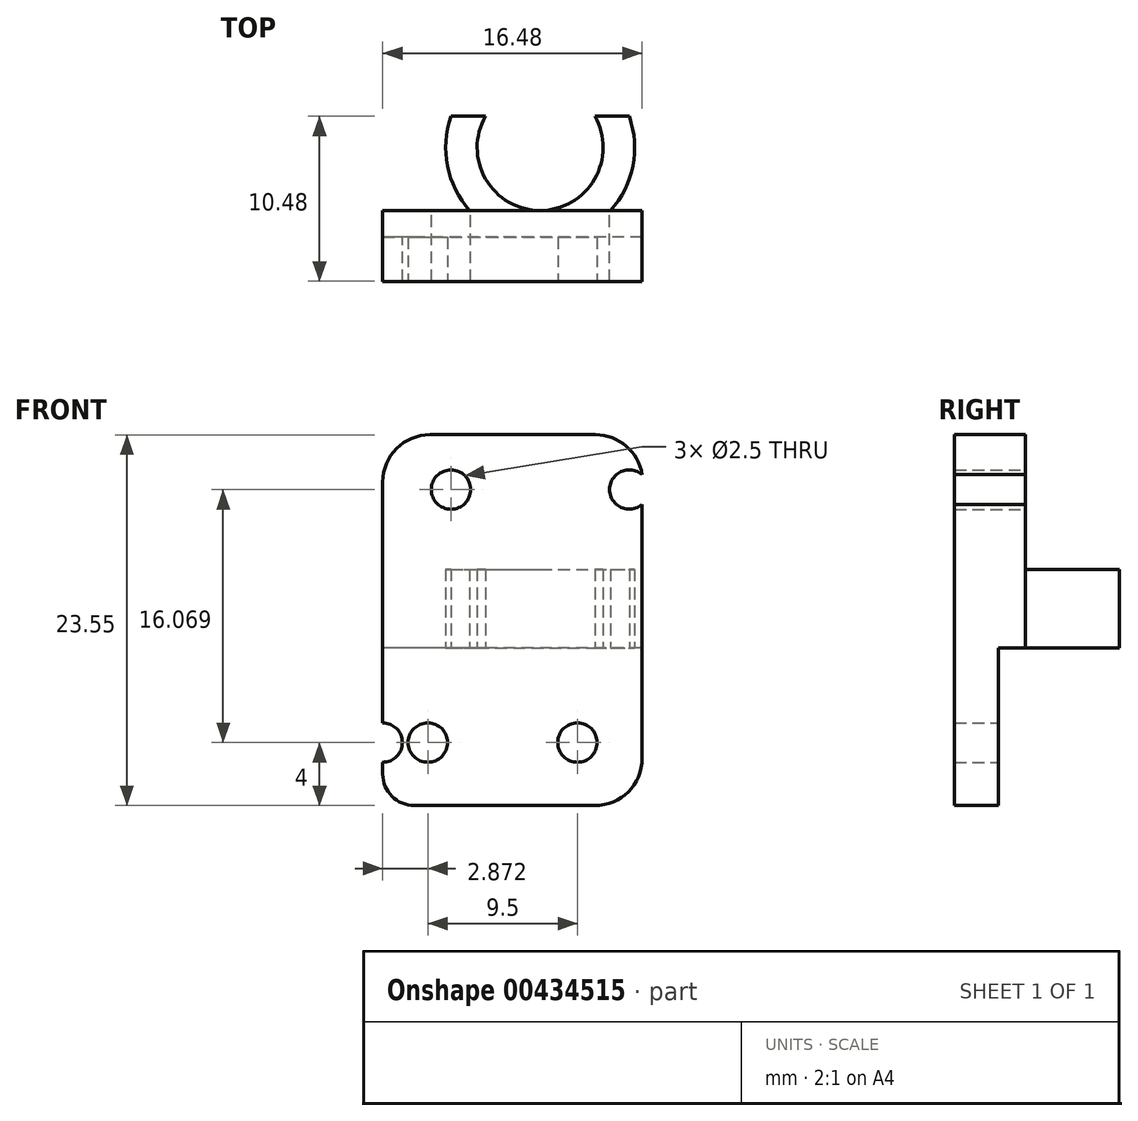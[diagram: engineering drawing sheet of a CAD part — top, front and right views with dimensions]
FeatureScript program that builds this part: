
annotation { "Feature Type Name" : "Feature", "Feature Type Description" : "" }
export const myFeature = defineFeature(function(context is Context, id is Id, definition is map)
    precondition{}
    {
        {
            var Q0;
            Q0=qCreatedBy(makeId("Top.planeOp"),FACE);
            var sketch = newSketch(context, id + "F0", { "sketchPlane" : qUnion([Q0])});
            skArc(sketch, "E0", {"start": v(-19.61, 7.8) * mm, "mid": v(-13.95, -0.17) * mm, "end": v(-8.28, 7.8) * mm});
            skLineSegment(sketch, "E1.right", {"start": v(278.54, 89.36) * mm, "end": v(278.54, 0) * mm});
            skArc(sketch, "E2", {"start": v(-17.42, 7.8) * mm, "mid": v(-13.95, 1.83) * mm, "end": v(-10.47, 7.8) * mm});
            skLineSegment(sketch, "E3.top", {"start": v(-19.61, 7.8) * mm, "end": v(-17.42, 7.8) * mm});
            skLineSegment(sketch, "E4.trimOffspring", {"start": v(-10.47, 7.8) * mm, "end": v(-8.28, 7.8) * mm});
            skPoint(sketch, "E5", {"position": v(-13.95, -1.45) * mm});
            skLineSegment(sketch, "E6", {"start": v(-13.95, 7.55) * mm, "end": v(-13.95, -10.44) * mm, "construction": true});
            skPoint(sketch, "E7.startSnap0", {"position": v(-13.95, 1.83) * mm});
            skSolve(sketch);
        }
        {
            var Q0;
            Q0=qSketchRegion(id+"F0",true);
            extrude(context, id + "F1", {"entities" : qUnion([Q0]), "depth" : 20 * mm});
        }
        {
            var Q0;
            Q0=qCreatedBy(makeId("Top.planeOp"),FACE);
            var sketch = newSketch(context, id + "F2", { "sketchPlane" : qUnion([Q0])});
            skArc(sketch, "E8.0.0", {"start": v(-17.42, 7.8) * mm, "mid": v(-13.95, 1.83) * mm, "end": v(-10.47, 7.8) * mm, "construction": true});
            skLineSegment(sketch, "E8.0.1", {"start": v(-10.47, 7.8) * mm, "end": v(-8.28, 7.8) * mm, "construction": true});
            skArc(sketch, "E8.0.2", {"start": v(-8.28, 7.8) * mm, "mid": v(-13.95, -0.17) * mm, "end": v(-19.61, 7.8) * mm, "construction": true});
            skLineSegment(sketch, "E8.0.3", {"start": v(-19.61, 7.8) * mm, "end": v(-17.42, 7.8) * mm, "construction": true});
            skPoint(sketch, "E9", {"position": v(-13.95, -0.17) * mm});
            skPoint(sketch, "E10", {"position": v(-13.95, 1.83) * mm});
            skLineSegment(sketch, "E11", {"start": v(-13.95, 1.83) * mm, "end": v(-3.95, 1.83) * mm});
            skLineSegment(sketch, "E12", {"start": v(-3.95, 1.83) * mm, "end": v(-3.95, -1.17) * mm});
            skLineSegment(sketch, "E13", {"start": v(-3.95, -1.17) * mm, "end": v(-23.95, -1.17) * mm});
            skLineSegment(sketch, "E14", {"start": v(-23.95, -1.17) * mm, "end": v(-23.95, 1.83) * mm});
            skLineSegment(sketch, "E15", {"start": v(-23.95, 1.83) * mm, "end": v(-13.95, 1.83) * mm});
            skSolve(sketch);
        }
        {
            var Q0;
            Q0=makeQuery(id+"F2.imprint","IMPRINT",FACE,{"disambiguationData":[TD([[makeQuery(id+"F2.imprint","IMPRINT",EDGE,{"derivedFrom":sQuery(id+"F2.wireOp",EDGE,"E11")}),-1.0]])]});
            extrude(context, id + "F3", {"entities" : qUnion([Q0]), "operationType" : NewBodyOperationType.ADD, "endBound" : BoundingType.SYMMETRIC, "depth" : 20 * mm});
        }
        {
            var Q0;
            Q0=qCreatedBy(makeId("Front.planeOp"),FACE);
            var sketch = newSketch(context, id + "F4", { "sketchPlane" : qUnion([Q0])});
            skCircle(sketch, "E16", {"center": v(-11.58, -6) * mm, "radius": 1.25 * mm});
            skPoint(sketch, "E17", {"position": v(-10.9, 30) * mm});
            skPoint(sketch, "E18.endSnap0", {"position": v(-14.04, 0) * mm});
            skLineSegment(sketch, "E19.0", {"start": v(-23.95, -10) * mm, "end": v(-3.95, -10) * mm, "construction": true});
            skPoint(sketch, "E20", {"position": v(-13.95, -10) * mm});
            skLineSegment(sketch, "E21", {"start": v(-13.95, -10) * mm, "end": v(-13.95, -0.98) * mm, "construction": true});
            skCircle(sketch, "E22.MirrorC", {"center": v(-21.08, -6) * mm, "radius": 1.25 * mm});
            skLineSegment(sketch, "E23", {"start": v(-21.08, -6) * mm, "end": v(-1.03, -6) * mm, "construction": true});
            skSolve(sketch);
        }
        {
            var Q0;
            Q0=qSketchRegion(id+"F4",true);
            extrude(context, id + "F5", {"entities" : qUnion([Q0]), "operationType" : NewBodyOperationType.REMOVE, "endBound" : BoundingType.SYMMETRIC, "oppositeDirection" : true, "depth" : 4.4 * mm});
        }
        {
            var Q0;
            Q0=makeQuery(id+"F3.opExtrude","CAP_FACE",FACE,{"disambiguationData":[OSD([sQuery(id+"F2.wireOp",EDGE,"E11"),sQuery(id+"F2.wireOp",EDGE,"E12"),sQuery(id+"F2.wireOp",EDGE,"E13"),sQuery(id+"F2.wireOp",EDGE,"E14"),sQuery(id+"F2.wireOp",EDGE,"E15")])],"isStart":false});
            var sketch = newSketch(context, id + "F6", { "sketchPlane" : qUnion([Q0])});
            skArc(sketch, "E24.0.0", {"start": v(-9.48, 1.83) * mm, "mid": v(-13.95, -0.17) * mm, "end": v(-18.42, 1.83) * mm});
            skLineSegment(sketch, "E24.0.1", {"start": v(-18.42, 1.83) * mm, "end": v(-23.95, 1.83) * mm});
            skLineSegment(sketch, "E24.0.2", {"start": v(-23.95, 1.83) * mm, "end": v(-23.95, -1.17) * mm});
            skLineSegment(sketch, "E24.0.3", {"start": v(-23.95, -1.17) * mm, "end": v(-3.95, -1.17) * mm});
            skLineSegment(sketch, "E24.0.4", {"start": v(-3.95, -1.17) * mm, "end": v(-3.95, 1.83) * mm});
            skLineSegment(sketch, "E24.0.5", {"start": v(-3.95, 1.83) * mm, "end": v(-9.48, 1.83) * mm});
            skSolve(sketch);
        }
        {
            var Q0;
            Q0=qSketchRegion(id+"F6",true);
            var Q1;
            Q1=makeQuery(id+"F1.opExtrude","CAP_FACE",FACE,{"disambiguationData":[OSD([sQuery(id+"F0.wireOp",EDGE,"E0"),sQuery(id+"F0.wireOp",EDGE,"E2"),sQuery(id+"F0.wireOp",EDGE,"E3.top"),sQuery(id+"F0.wireOp",EDGE,"E4.trimOffspring")])],"isStart":false});
            extrude(context, id + "F7", {"entities" : qUnion([Q0]), "operationType" : NewBodyOperationType.ADD, "endBound" : BoundingType.UP_TO_SURFACE, "endBoundEntityFace" : qUnion([Q1]), "depth" : 6.4 * mm});
        }
        {
            var Q0;
            Q0=makeQuery(id+"F7.boolean.opBoolean","MERGE",FACE,{"derivedFrom":[makeQuery(id+"F3.opExtrude","SWEPT_FACE",FACE,{"disambiguationData":[OSD([sQuery(id+"F2.wireOp",EDGE,"E11"),sQuery(id+"F2.wireOp",EDGE,"E15")])]}),makeQuery(id+"F7.opExtrude","SWEPT_FACE",FACE,{"disambiguationData":[OSD([sQuery(id+"F6.wireOp",EDGE,"E24.0.1")])]}),makeQuery(id+"F7.opExtrude","SWEPT_FACE",FACE,{"disambiguationData":[OSD([sQuery(id+"F6.wireOp",EDGE,"E24.0.5")])]})]});
            cPlane(context, id + "F8", {"entities" : qUnion([Q0]), "cplaneType" : CPlaneType.OFFSET, "offset" : 25 * mm, "width" : 150 * mm, "height" : 150 * mm});
        }
        {
            var Q0;
            Q0=qCreatedBy(id+"F8.planeOp",FACE);
            var sketch = newSketch(context, id + "F9", { "sketchPlane" : qUnion([Q0])});
            skPoint(sketch, "E25.0", {"position": v(21.08, -6) * mm});
            skPoint(sketch, "E26.0", {"position": v(11.58, -6) * mm});
            skLineSegment(sketch, "E27", {"start": v(1.82, -6) * mm, "end": v(28.97, -6) * mm, "construction": true});
            skLineSegment(sketch, "E28.0", {"start": v(3.95, 20) * mm, "end": v(3.95, -10) * mm, "construction": true});
            skLineSegment(sketch, "E29.0", {"start": v(23.95, 20) * mm, "end": v(23.95, -10) * mm, "construction": true});
            skPoint(sketch, "E30", {"position": v(3.95, -6) * mm});
            skPoint(sketch, "E31", {"position": v(23.95, -6) * mm});
            skCircle(sketch, "E32.0", {"center": v(11.58, -6) * mm, "radius": 1.25 * mm, "construction": true});
            skCircle(sketch, "E33", {"center": v(23.95, -6) * mm, "radius": 1.25 * mm});
            skCircle(sketch, "E34.MirrorC", {"center": v(3.95, -6) * mm, "radius": 1.25 * mm});
            skSolve(sketch);
        }
        {
            var Q0;
            Q0=qSketchRegion(id+"F9",true);
            extrude(context, id + "F10", {"entities" : qUnion([Q0]), "operationType" : NewBodyOperationType.REMOVE, "endBound" : BoundingType.THROUGH_ALL, "oppositeDirection" : true, "depth" : 25 * mm});
        }
        {
            var Q0;
            Q0=makeQuery(id+"F3.opExtrude","CAP_EDGE",EDGE,{"disambiguationData":[OSD([sQuery(id+"F2.wireOp",EDGE,"E14")])],"isStart":true});
            var Q1;
            Q1=makeQuery(id+"F3.opExtrude","CAP_EDGE",EDGE,{"disambiguationData":[OSD([sQuery(id+"F2.wireOp",EDGE,"E12")])],"isStart":true});
            fillet(context, id + "F11", {"entities" : qUnion([Q0, Q1]), "radius" : 2 * mm, "tangentPropagation" : true, "allowEdgeOverflow" : false});
        }
        {
            var Q0;
            Q0=makeQuery(id+"F7.boolean.opBoolean","MERGE",FACE,{"derivedFrom":[makeQuery(id+"F3.opExtrude","SWEPT_FACE",FACE,{"disambiguationData":[OSD([sQuery(id+"F2.wireOp",EDGE,"E13")])]}),makeQuery(id+"F7.opExtrude","SWEPT_FACE",FACE,{"disambiguationData":[OSD([sQuery(id+"F6.wireOp",EDGE,"E24.0.3")])]})]});
            cPlane(context, id + "F12", {"entities" : qUnion([Q0]), "cplaneType" : CPlaneType.OFFSET, "offset" : 0 * mm, "width" : 150 * mm, "height" : 150 * mm});
        }
        {
            var Q0;
            Q0=qCreatedBy(id+"F12.planeOp",FACE);
            var sketch = newSketch(context, id + "F13", { "sketchPlane" : qUnion([Q0])});
            skLineSegment(sketch, "E35.0.0", {"start": v(-23.95, -7.25) * mm, "end": v(-23.95, -8) * mm});
            skArc(sketch, "E35.0.1", {"start": v(-23.95, -8) * mm, "mid": v(-23.36, -9.41) * mm, "end": v(-21.95, -10) * mm});
            skLineSegment(sketch, "E35.0.2", {"start": v(-21.95, -10) * mm, "end": v(-5.95, -10) * mm});
            skArc(sketch, "E35.0.3", {"start": v(-5.95, -10) * mm, "mid": v(-4.53, -9.41) * mm, "end": v(-3.95, -8) * mm});
            skLineSegment(sketch, "E35.0.4", {"start": v(-3.95, -8) * mm, "end": v(-3.95, -7.25) * mm});
            skArc(sketch, "E35.0.5", {"start": v(-3.95, -7.25) * mm, "mid": v(-5.2, -6) * mm, "end": v(-3.95, -4.75) * mm});
            skLineSegment(sketch, "E35.0.6", {"start": v(-3.95, -4.75) * mm, "end": v(-3.95, 20) * mm});
            skLineSegment(sketch, "E35.0.7", {"start": v(-3.95, 20) * mm, "end": v(-23.95, 20) * mm});
            skLineSegment(sketch, "E35.0.8", {"start": v(-23.95, 20) * mm, "end": v(-23.95, -4.75) * mm});
            skArc(sketch, "E35.0.9", {"start": v(-23.95, -4.75) * mm, "mid": v(-22.7, -6) * mm, "end": v(-23.95, -7.25) * mm});
            skSolve(sketch);
        }
        {
            var Q0;
            Q0=qSketchRegion(id+"F13",true);
            extrude(context, id + "F14", {"entities" : qUnion([Q0]), "operationType" : NewBodyOperationType.ADD, "depth" : 1.5 * mm});
        }
        {
            var Q0;
            Q0=makeQuery(id+"F7.boolean.opBoolean","MERGE",FACE,{"derivedFrom":[makeQuery(id+"F3.opExtrude","SWEPT_FACE",FACE,{"disambiguationData":[OSD([sQuery(id+"F2.wireOp",EDGE,"E11"),sQuery(id+"F2.wireOp",EDGE,"E15")])]}),makeQuery(id+"F7.opExtrude","SWEPT_FACE",FACE,{"disambiguationData":[OSD([sQuery(id+"F6.wireOp",EDGE,"E24.0.1")])]}),makeQuery(id+"F7.opExtrude","SWEPT_FACE",FACE,{"disambiguationData":[OSD([sQuery(id+"F6.wireOp",EDGE,"E24.0.5")])]})]});
            cPlane(context, id + "F15", {"entities" : qUnion([Q0]), "cplaneType" : CPlaneType.OFFSET, "offset" : 0 * mm, "width" : 150 * mm, "height" : 150 * mm});
        }
        {
            var Q0;
            Q0=qCreatedBy(id+"F8.planeOp",FACE);
            var sketch = newSketch(context, id + "F16", { "sketchPlane" : qUnion([Q0])});
            skPoint(sketch, "E36.0", {"position": v(3.95, 0) * mm});
            skPoint(sketch, "E37.0", {"position": v(23.95, 0) * mm});
            skPoint(sketch, "E38.0", {"position": v(23.95, -10) * mm});
            skPoint(sketch, "E39.0", {"position": v(3.95, -10) * mm});
            skLineSegment(sketch, "E40", {"start": v(3.95, 0) * mm, "end": v(23.95, 0) * mm});
            skLineSegment(sketch, "E41", {"start": v(23.95, 0) * mm, "end": v(23.95, -10) * mm});
            skLineSegment(sketch, "E42", {"start": v(23.95, -10) * mm, "end": v(3.95, -10) * mm});
            skLineSegment(sketch, "E43", {"start": v(3.95, -10) * mm, "end": v(3.95, 0) * mm});
            skSolve(sketch);
        }
        {
            var Q0;
            Q0=qSketchRegion(id+"F16",true);
            extrude(context, id + "F17", {"entities" : qUnion([Q0]), "operationType" : NewBodyOperationType.REMOVE, "oppositeDirection" : true, "depth" : 26.7 * mm});
        }
        {
            var Q0;
            Q0=qCreatedBy(makeId("Front.planeOp"),FACE);
            cPlane(context, id + "F18", {"entities" : qUnion([Q0]), "cplaneType" : CPlaneType.OFFSET, "offset" : 25 * mm, "width" : 150 * mm, "height" : 150 * mm});
        }
        {
            var Q0;
            Q0=qCreatedBy(id+"F18.planeOp",FACE);
            var sketch = newSketch(context, id + "F19", { "sketchPlane" : qUnion([Q0])});
            skCircle(sketch, "E44.0", {"center": v(-11.58, -6) * mm, "radius": 1.25 * mm});
            skCircle(sketch, "E45.0", {"center": v(-21.08, -6) * mm, "radius": 1.25 * mm});
            skSolve(sketch);
        }
        {
            var Q0;
            Q0=qSketchRegion(id+"F19",true);
            extrude(context, id + "F20", {"entities" : qUnion([Q0]), "operationType" : NewBodyOperationType.REMOVE, "oppositeDirection" : true, "depth" : 32.1 * mm});
        }
        {
            var Q0;
            Q0=qCreatedBy(makeId("Top.planeOp"),FACE);
            cPlane(context, id + "F21", {"entities" : qUnion([Q0]), "cplaneType" : CPlaneType.OFFSET, "offset" : 11.9 * mm, "width" : 150 * mm, "height" : 150 * mm});
        }
        {
            var Q0;
            Q0=qCreatedBy(id+"F21.planeOp",FACE);
            var sketch = newSketch(context, id + "F22", { "sketchPlane" : qUnion([Q0])});
            skArc(sketch, "E46.0.0", {"start": v(-10.47, 7.8) * mm, "mid": v(-13.95, 1.83) * mm, "end": v(-17.42, 7.8) * mm, "construction": true});
            skLineSegment(sketch, "E46.0.1", {"start": v(-17.42, 7.8) * mm, "end": v(-19.61, 7.8) * mm, "construction": true});
            skArc(sketch, "E46.0.2", {"start": v(-19.61, 7.8) * mm, "mid": v(-19.83, 4.65) * mm, "end": v(-18.42, 1.83) * mm, "construction": true});
            skLineSegment(sketch, "E46.0.3", {"start": v(-18.42, 1.83) * mm, "end": v(-23.95, 1.83) * mm, "construction": true});
            skLineSegment(sketch, "E46.0.4", {"start": v(-23.95, 1.83) * mm, "end": v(-23.95, -2.67) * mm, "construction": true});
            skLineSegment(sketch, "E46.0.5", {"start": v(-23.95, -2.67) * mm, "end": v(-3.95, -2.67) * mm, "construction": true});
            skLineSegment(sketch, "E46.0.6", {"start": v(-3.95, -2.67) * mm, "end": v(-3.95, 1.83) * mm, "construction": true});
            skLineSegment(sketch, "E46.0.7", {"start": v(-3.95, 1.83) * mm, "end": v(-9.48, 1.83) * mm, "construction": true});
            skArc(sketch, "E46.0.8", {"start": v(-9.48, 1.83) * mm, "mid": v(-8.06, 4.65) * mm, "end": v(-8.28, 7.8) * mm, "construction": true});
            skLineSegment(sketch, "E46.0.9", {"start": v(-8.28, 7.8) * mm, "end": v(-10.47, 7.8) * mm, "construction": true});
            skLineSegment(sketch, "E47.bottom", {"start": v(-23.95, 1.83) * mm, "end": v(-3.95, 1.83) * mm});
            skLineSegment(sketch, "E47.top", {"start": v(-23.95, 11.1) * mm, "end": v(-3.95, 11.1) * mm});
            skLineSegment(sketch, "E47.left", {"start": v(-23.95, 1.83) * mm, "end": v(-23.95, 11.1) * mm});
            skLineSegment(sketch, "E47.right", {"start": v(-3.95, 1.83) * mm, "end": v(-3.95, 11.1) * mm});
            skSolve(sketch);
        }
        {
            var Q0;
            Q0=qSketchRegion(id+"F22",true);
            extrude(context, id + "F23", {"entities" : qUnion([Q0]), "operationType" : NewBodyOperationType.REMOVE, "oppositeDirection" : true, "depth" : 6.9 * mm});
        }
        {
            var Q0;
            Q0=qSketchRegion(id+"F22",true);
            extrude(context, id + "F24", {"entities" : qUnion([Q0]), "operationType" : NewBodyOperationType.REMOVE, "depth" : 2.9 * mm});
        }
        {
            var Q0;
            Q0=qCreatedBy(id+"F15.planeOp",FACE);
            var sketch = newSketch(context, id + "F25", { "sketchPlane" : qUnion([Q0])});
            skLineSegment(sketch, "E48.0", {"start": v(23.95, 11.9) * mm, "end": v(3.95, 11.9) * mm, "construction": true});
            skPoint(sketch, "E49.0", {"position": v(8.28, 11.9) * mm});
            skLineSegment(sketch, "E50", {"start": v(8.28, 14.8) * mm, "end": v(8.28, 5.33) * mm, "construction": true});
            skLineSegment(sketch, "E51", {"start": v(13.95, 14.95) * mm, "end": v(13.95, 5.19) * mm, "construction": true});
            skPoint(sketch, "E51.startSnap0", {"position": v(13.95, 11.9) * mm});
            skCircle(sketch, "E52", {"center": v(8.28, 10.07) * mm, "radius": 1.25 * mm});
            skCircle(sketch, "E53.MirrorC", {"center": v(19.61, 10.07) * mm, "radius": 1.25 * mm});
            skSolve(sketch);
        }
        {
            var Q0;
            Q0=qSketchRegion(id+"F25",true);
            extrude(context, id + "F26", {"entities" : qUnion([Q0]), "operationType" : NewBodyOperationType.REMOVE, "endBound" : BoundingType.SYMMETRIC, "oppositeDirection" : true, "depth" : 25 * mm});
        }
        {
            var Q0;
            Q0=qCreatedBy(id+"F8.planeOp",FACE);
            var sketch = newSketch(context, id + "F27", { "sketchPlane" : qUnion([Q0])});
            skLineSegment(sketch, "E54.bottom", {"start": v(-7.7, 30.73) * mm, "end": v(7.47, 30.73) * mm});
            skLineSegment(sketch, "E54.top", {"start": v(-7.7, -20.78) * mm, "end": v(7.47, -20.78) * mm});
            skLineSegment(sketch, "E54.left", {"start": v(-7.7, 30.73) * mm, "end": v(-7.7, -20.78) * mm});
            skLineSegment(sketch, "E54.right", {"start": v(7.47, 30.73) * mm, "end": v(7.47, -20.78) * mm});
            skSolve(sketch);
        }
        {
            var Q0;
            Q0 = qSketchRegion(id + "F27", true);
            extrude(context, id + "F28", {"entities" : qUnion([Q0]), "operationType" : NewBodyOperationType.REMOVE, "oppositeDirection" : true, "depth" : 40.7 * mm});
        }
        {
            var Q0;
            {var subQ0=sQuery(id+"F22.wireOp",EDGE,"E47.bottom");var subQ11=makeQuery(id+"F7.boolean.opBoolean","MERGE",FACE,{"derivedFrom":[makeQuery(id+"F3.opExtrude","SWEPT_FACE",FACE,{"disambiguationData":[OSD([sQuery(id+"F2.wireOp",EDGE,"E11"),sQuery(id+"F2.wireOp",EDGE,"E15")])]}),makeQuery(id+"F7.opExtrude","SWEPT_FACE",FACE,{"disambiguationData":[OSD([sQuery(id+"F6.wireOp",EDGE,"E24.0.1")])]}),makeQuery(id+"F7.opExtrude","SWEPT_FACE",FACE,{"disambiguationData":[OSD([sQuery(id+"F6.wireOp",EDGE,"E24.0.5")])]})]});Q0=makeQuery(id+"F24.boolean.opBoolean","MERGE",FACE,{"derivedFrom":[makeQuery(id+"F23.boolean.opBoolean","MERGE",FACE,{"derivedFrom":[makeQuery(id+"F17.boolean.opBoolean","SPLIT",FACE,{"disambiguationData":[TD([makeQuery(id+"F3.opExtrude","SWEPT_FACE",FACE,{"disambiguationData":[OSD([sQuery(id+"F2.wireOp",EDGE,"E14")])]})])],"derivedFrom":subQ11}),makeQuery(id+"F17.boolean.opBoolean","SPLIT",FACE,{"disambiguationData":[TD([makeQuery(id+"F3.opExtrude","SWEPT_FACE",FACE,{"disambiguationData":[OSD([sQuery(id+"F2.wireOp",EDGE,"E12")])]})])],"derivedFrom":subQ11}),makeQuery(id+"F23.opExtrude","SWEPT_FACE",FACE,{"disambiguationData":[OSD([subQ0])]})]}),makeQuery(id+"F24.opExtrude","SWEPT_FACE",FACE,{"disambiguationData":[OSD([subQ0])]})]});}
            var sketch = newSketch(context, id + "F29", { "sketchPlane" : qUnion([Q0])});
            skLineSegment(sketch, "E55.bottom", {"start": v(-1.27, 32.7) * mm, "end": v(33.98, 32.7) * mm});
            skLineSegment(sketch, "E55.top", {"start": v(-1.27, 13.55) * mm, "end": v(33.98, 13.55) * mm});
            skLineSegment(sketch, "E55.left", {"start": v(-1.27, 32.7) * mm, "end": v(-1.27, 13.55) * mm});
            skLineSegment(sketch, "E55.right", {"start": v(33.98, 32.7) * mm, "end": v(33.98, 13.55) * mm});
            skSolve(sketch);
        }
        {
            var Q0;
            Q0 = qSketchRegion(id + "F29", true);
            extrude(context, id + "F30", {"entities" : qUnion([Q0]), "operationType" : NewBodyOperationType.REMOVE, "endBound" : BoundingType.SYMMETRIC, "depth" : 25 * mm});
        }
        {
            var Q0;
            Q0=makeQuery(id+"F28.boolean.opBoolean","INTERSECT",EDGE,{"derivedFrom":[makeQuery(id+"F14.boolean.opBoolean","MERGE",FACE,{"derivedFrom":[makeQuery(id+"F3.opExtrude","CAP_FACE",FACE,{"disambiguationData":[OSD([sQuery(id+"F2.wireOp",EDGE,"E11"),sQuery(id+"F2.wireOp",EDGE,"E12"),sQuery(id+"F2.wireOp",EDGE,"E13"),sQuery(id+"F2.wireOp",EDGE,"E14"),sQuery(id+"F2.wireOp",EDGE,"E15")])],"isStart":true}),makeQuery(id+"F14.opExtrude","SWEPT_FACE",FACE,{"disambiguationData":[OSD([sQuery(id+"F13.wireOp",EDGE,"E35.0.2")])]})]}),makeQuery(id+"F28.opExtrude","SWEPT_FACE",FACE,{"disambiguationData":[OSD([sQuery(id+"F27.wireOp",EDGE,"E54.right")])]})]});
            var Q1;
            {var subQ0=sQuery(id+"F0.wireOp",EDGE,"E4.trimOffspring");var subQ1=sQuery(id+"F0.wireOp",EDGE,"E3.top");var subQ2=sQuery(id+"F0.wireOp",EDGE,"E2");var subQ3=sQuery(id+"F0.wireOp",EDGE,"E0");Q1=makeQuery(id+"F30.boolean.opBoolean","INTERSECT",EDGE,{"derivedFrom":[makeQuery(id+"F14.boolean.opBoolean","MERGE",FACE,{"derivedFrom":[makeQuery(id+"F10.boolean.opBoolean","SPLIT",FACE,{"disambiguationData":[TD([makeQuery(id+"F1.opExtrude","CAP_FACE",FACE,{"disambiguationData":[OSD([subQ3,subQ2,subQ1,subQ0])],"isStart":false})])],"derivedFrom":makeQuery(id+"F7.boolean.opBoolean","MERGE",FACE,{"derivedFrom":[makeQuery(id+"F3.opExtrude","SWEPT_FACE",FACE,{"disambiguationData":[OSD([sQuery(id+"F2.wireOp",EDGE,"E14")])]}),makeQuery(id+"F7.opExtrude","SWEPT_FACE",FACE,{"disambiguationData":[OSD([sQuery(id+"F6.wireOp",EDGE,"E24.0.2")])]})]})}),makeQuery(id+"F14.opExtrude","SWEPT_FACE",FACE,{"disambiguationData":[OSD([sQuery(id+"F13.wireOp",EDGE,"E35.0.8")])]})]}),makeQuery(id+"F30.opExtrude","SWEPT_FACE",FACE,{"disambiguationData":[OSD([sQuery(id+"F29.wireOp",EDGE,"E55.top")])]})]});}
            var Q2;
            {var subQ5=sQuery(id+"F13.wireOp",EDGE,"E35.0.7");Q2=makeQuery(id+"F30.boolean.opBoolean","INTERSECT",EDGE,{"derivedFrom":[makeQuery(id+"F28.boolean.opBoolean","COPY",FACE,{"disambiguationData":[TD([makeQuery(id+"F14.opExtrude","SWEPT_FACE",FACE,{"disambiguationData":[OSD([subQ5])]})])],"derivedFrom":makeQuery(id+"F28.opExtrude","SWEPT_FACE",FACE,{"disambiguationData":[OSD([sQuery(id+"F27.wireOp",EDGE,"E54.right")])]})}),makeQuery(id+"F30.opExtrude","SWEPT_FACE",FACE,{"disambiguationData":[OSD([sQuery(id+"F29.wireOp",EDGE,"E55.top")])]})]});}
            fillet(context, id + "F31", {"entities" : qUnion([Q0, Q1, Q2]), "radius" : 3 * mm, "tangentPropagation" : true, "allowEdgeOverflow" : false});
        }
    });
